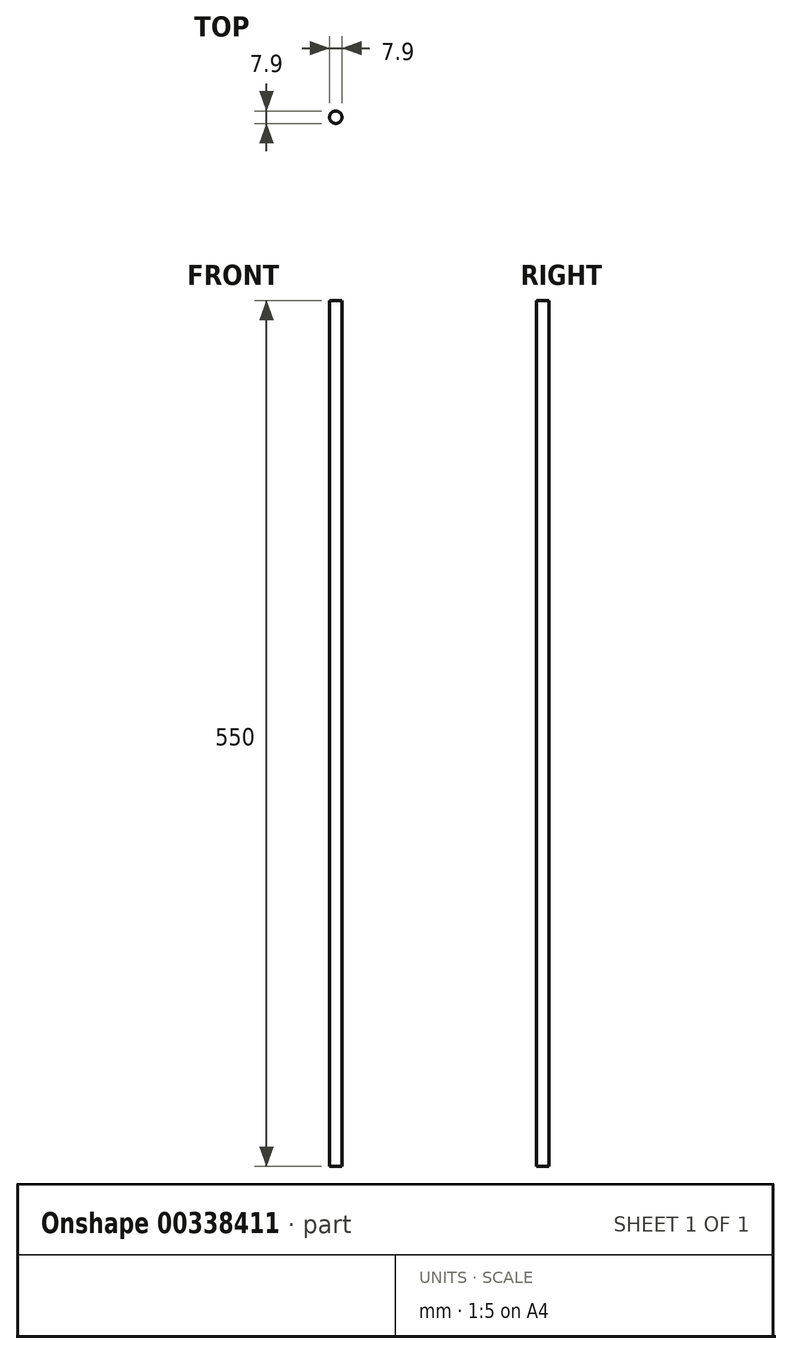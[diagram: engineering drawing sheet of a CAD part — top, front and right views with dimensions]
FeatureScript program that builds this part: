
annotation { "Feature Type Name" : "Feature", "Feature Type Description" : "" }
export const myFeature = defineFeature(function(context is Context, id is Id, definition is map)
    precondition{}
    {
        {
            var Q0;
            Q0=qCreatedBy(makeId("Top.planeOp"),FACE);
            var sketch = newSketch(context, id + "F0", { "sketchPlane" : qUnion([Q0])});
            skCircle(sketch, "E0", {"center": v(0, 0) * mm, "radius": 3.95 * mm});
            skSolve(sketch);
        }
        {
            var Q0;
            Q0 = qSketchRegion(id + "F0", true);
            extrude(context, id + "F1", {"entities" : qUnion([Q0]), "depth" : 550 * mm, "symmetric" : true});
        }
    });
